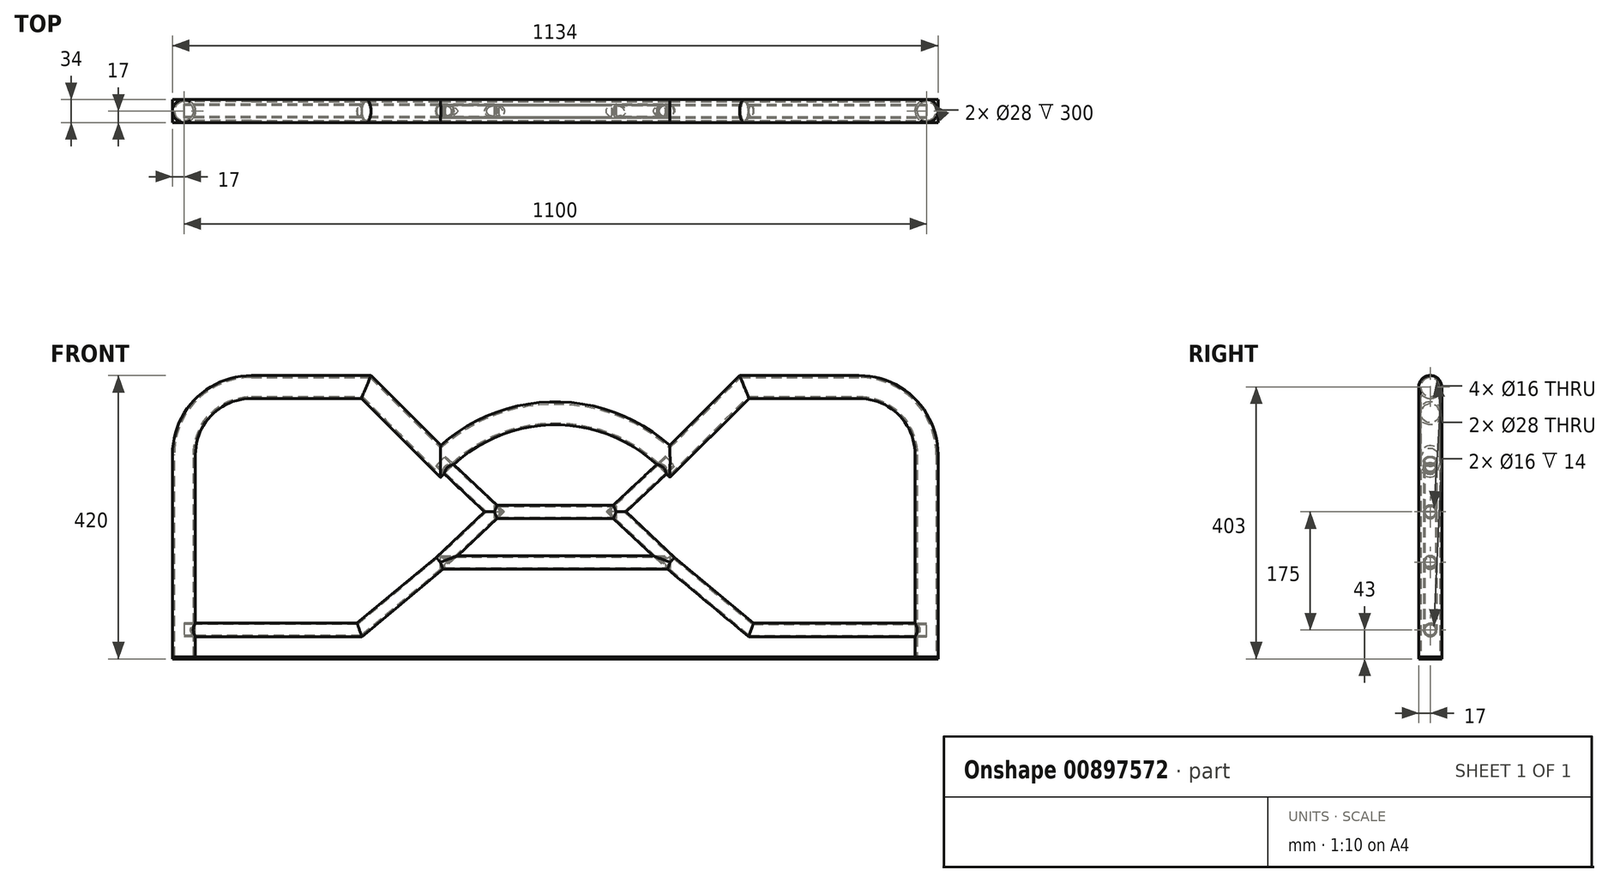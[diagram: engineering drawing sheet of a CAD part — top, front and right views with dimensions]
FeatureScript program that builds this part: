
annotation { "Feature Type Name" : "Feature", "Feature Type Description" : "" }
export const myFeature = defineFeature(function(context is Context, id is Id, definition is map)
    precondition{}
    {
        {
            var Q0;
            Q0=qCreatedBy(makeId("Front.planeOp"),FACE);
            var sketch = newSketch(context, id + "F0", { "sketchPlane" : qUnion([Q0])});
            skLineSegment(sketch, "E0", {"start": v(0, 0) * mm, "end": v(1100, 0) * mm, "construction": true});
            skLineSegment(sketch, "E1", {"start": v(0, 0) * mm, "end": v(0, 300) * mm});
            skLineSegment(sketch, "E2", {"start": v(1100, 0) * mm, "end": v(1100, 300) * mm});
            skLineSegment(sketch, "E3", {"start": v(550, 400) * mm, "end": v(550, 0) * mm, "construction": true});
            skLineSegment(sketch, "E4", {"start": v(550, 290) * mm, "end": v(380, 290) * mm, "construction": true});
            skLineSegment(sketch, "E5", {"start": v(550, 290) * mm, "end": v(720, 290) * mm, "construction": true});
            skLineSegment(sketch, "E6", {"start": v(380, 290) * mm, "end": v(270, 400) * mm});
            skArc(sketch, "E7", {"start": v(720, 290) * mm, "mid": v(550, 361) * mm, "end": v(380, 290) * mm});
            skLineSegment(sketch, "E8.MirrorCS", {"start": v(720, 290) * mm, "end": v(830, 400) * mm});
            skLineSegment(sketch, "E9", {"start": v(550, 140) * mm, "end": v(380, 140) * mm});
            skLineSegment(sketch, "E10", {"start": v(550, 140) * mm, "end": v(720, 140) * mm});
            skLineSegment(sketch, "E11", {"start": v(380, 140) * mm, "end": v(260, 40) * mm});
            skLineSegment(sketch, "E12", {"start": v(720, 140) * mm, "end": v(840, 40) * mm});
            skLineSegment(sketch, "E13", {"start": v(260, 40) * mm, "end": v(0, 40) * mm});
            skLineSegment(sketch, "E14", {"start": v(840, 40) * mm, "end": v(1100, 40) * mm});
            skLineSegment(sketch, "E15", {"start": v(100, 400) * mm, "end": v(270, 400) * mm});
            skLineSegment(sketch, "E16", {"start": v(1000, 400) * mm, "end": v(830, 400) * mm});
            skLineSegment(sketch, "E17", {"start": v(270, 400) * mm, "end": v(830, 400) * mm, "construction": true});
            skPoint(sketch, "E18.visualSharp", {"position": v(0, 400) * mm});
            skArc(sketch, "E18.filletArc", {"start": v(100, 400) * mm, "mid": v(29.29, 370.71) * mm, "end": v(0, 300) * mm});
            skPoint(sketch, "E19.visualSharp", {"position": v(1100, 400) * mm});
            skArc(sketch, "E19.filletArc", {"start": v(1100, 300) * mm, "mid": v(1070.71, 370.71) * mm, "end": v(1000, 400) * mm});
            skLineSegment(sketch, "E20", {"start": v(550, 215) * mm, "end": v(640, 215) * mm});
            skLineSegment(sketch, "E21", {"start": v(550, 215) * mm, "end": v(460, 215) * mm});
            skLineSegment(sketch, "E22", {"start": v(380, 290) * mm, "end": v(460, 215) * mm});
            skLineSegment(sketch, "E23", {"start": v(380, 140) * mm, "end": v(460, 215) * mm});
            skLineSegment(sketch, "E24", {"start": v(720, 290) * mm, "end": v(640, 215) * mm});
            skLineSegment(sketch, "E25", {"start": v(720, 140) * mm, "end": v(640, 215) * mm});
            skSolve(sketch);
        }
        {
            var Q0;
            Q0=sQuery(id+"F0.wireOp",EDGE,"E1");
            cPlane(context, id + "F1", {"entities" : qUnion([Q0]), "cplaneType" : CPlaneType.MID_PLANE, "offset" : 25 * mm, "width" : 150 * mm, "height" : 150 * mm});
        }
        {
            var Q0;
            Q0=qCreatedBy(id+"F1.planeOp",FACE);
            var sketch = newSketch(context, id + "F2", { "sketchPlane" : qUnion([Q0])});
            skCircle(sketch, "E26", {"center": v(0, 0) * mm, "radius": 17 * mm});
            skCircle(sketch, "E27", {"center": v(0, 0) * mm, "radius": 14 * mm});
            skSolve(sketch);
        }
        {
            var Q0;
            Q0=makeQuery(id+"F2.imprint","IMPRINT",FACE,{"disambiguationData":[TD([[makeQuery(id+"F2.imprint","IMPRINT",EDGE,{"derivedFrom":sQuery(id+"F2.wireOp",EDGE,"E26")}),1.0]])]});
            var Q1;
            Q1=sQuery(id+"F0.wireOp",EDGE,"E1");
            var Q2;
            Q2=sQuery(id+"F0.wireOp",EDGE,"E18.filletArc");
            var Q3;
            Q3=sQuery(id+"F0.wireOp",EDGE,"E15");
            var Q4;
            Q4=sQuery(id+"F0.wireOp",EDGE,"E6");
            var Q5;
            Q5=sQuery(id+"F0.wireOp",EDGE,"E7");
            var Q6;
            Q6=sQuery(id+"F0.wireOp",EDGE,"E8.MirrorCS");
            var Q7;
            Q7=sQuery(id+"F0.wireOp",EDGE,"E16");
            var Q8;
            Q8=sQuery(id+"F0.wireOp",EDGE,"E19.filletArc");
            var Q9;
            Q9=sQuery(id+"F0.wireOp",EDGE,"E2");
            sweep(context, id + "F3", {"profiles" : qUnion([Q0]), "path" : qUnion([Q1, Q2, Q3, Q4, Q5, Q6, Q7, Q8, Q9])});
        }
        {
            var Q0;
            Q0=sQuery(id+"F0.wireOp",EDGE,"E13");
            cPlane(context, id + "F4", {"entities" : qUnion([Q0]), "cplaneType" : CPlaneType.MID_PLANE, "offset" : 25 * mm, "width" : 150 * mm, "height" : 150 * mm});
        }
        {
            var Q0;
            Q0=qCreatedBy(id+"F4.planeOp",FACE);
            var sketch = newSketch(context, id + "F5", { "sketchPlane" : qUnion([Q0])});
            skCircle(sketch, "E28", {"center": v(0, 40) * mm, "radius": 10 * mm});
            skCircle(sketch, "E29", {"center": v(0, 40) * mm, "radius": 8 * mm});
            skSolve(sketch);
        }
        {
            var Q0;
            Q0=makeQuery(id+"F5.imprint","IMPRINT",FACE,{"disambiguationData":[TD([[makeQuery(id+"F5.imprint","IMPRINT",EDGE,{"derivedFrom":sQuery(id+"F5.wireOp",EDGE,"E28")}),1.0]])]});
            var Q1;
            Q1=sQuery(id+"F0.wireOp",EDGE,"E13");
            var Q2;
            Q2=sQuery(id+"F0.wireOp",EDGE,"E11");
            var Q3;
            Q3=sQuery(id+"F0.wireOp",EDGE,"E23");
            var Q4;
            Q4=sQuery(id+"F0.wireOp",EDGE,"E22");
            sweep(context, id + "F6", {"profiles" : qUnion([Q0]), "path" : qUnion([Q1, Q2, Q3, Q4])});
        }
        {
            var Q0;
            Q0=sQuery(id+"F0.wireOp",EDGE,"E14");
            cPlane(context, id + "F7", {"entities" : qUnion([Q0]), "cplaneType" : CPlaneType.MID_PLANE, "offset" : 25 * mm, "width" : 150 * mm, "height" : 150 * mm});
        }
        {
            var Q0;
            Q0=sQuery(id+"F0.wireOp",VERTEX,"E9.start");
            var Q1;
            Q1=sQuery(id+"F0.wireOp",EDGE,"E10");
            cPlane(context, id + "F8", {"entities" : qUnion([Q0, Q1]), "cplaneType" : CPlaneType.LINE_POINT, "offset" : 25 * mm, "width" : 150 * mm, "height" : 150 * mm});
        }
        {
            var Q0;
            Q0=qCreatedBy(id+"F8.planeOp",FACE);
            var sketch = newSketch(context, id + "F9", { "sketchPlane" : qUnion([Q0])});
            skCircle(sketch, "E30", {"center": v(0, 140) * mm, "radius": 10 * mm});
            skCircle(sketch, "E31", {"center": v(0, 140) * mm, "radius": 8 * mm});
            skSolve(sketch);
        }
        {
            var Q0;
            Q0=makeQuery(id+"F9.imprint","IMPRINT",FACE,{"disambiguationData":[TD([[makeQuery(id+"F9.imprint","IMPRINT",EDGE,{"derivedFrom":sQuery(id+"F9.wireOp",EDGE,"E30")}),1.0]])]});
            var Q1;
            Q1=sQuery(id+"F0.wireOp",EDGE,"E9");
            var Q2;
            Q2=sQuery(id+"F0.wireOp",EDGE,"E10");
            sweep(context, id + "F10", {"operationType" : NewBodyOperationType.ADD, "profiles" : qUnion([Q0]), "path" : qUnion([Q1, Q2])});
        }
        {
            var Q0;
            Q0=qCreatedBy(id+"F8.planeOp",FACE);
            var sketch = newSketch(context, id + "F11", { "sketchPlane" : qUnion([Q0])});
            skCircle(sketch, "E32", {"center": v(0, 215) * mm, "radius": 10 * mm});
            skCircle(sketch, "E33", {"center": v(0, 215) * mm, "radius": 8 * mm});
            skSolve(sketch);
        }
        {
            var Q0;
            Q0=makeQuery(id+"F11.imprint","IMPRINT",FACE,{"disambiguationData":[TD([[makeQuery(id+"F11.imprint","IMPRINT",EDGE,{"derivedFrom":sQuery(id+"F11.wireOp",EDGE,"E32")}),1.0]])]});
            var Q1;
            Q1=sQuery(id+"F0.wireOp",EDGE,"E21");
            var Q2;
            Q2=sQuery(id+"F0.wireOp",EDGE,"E20");
            sweep(context, id + "F12", {"operationType" : NewBodyOperationType.ADD, "profiles" : qUnion([Q0]), "path" : qUnion([Q1, Q2])});
        }
        {
            var Q0;
            Q0=qCreatedBy(id+"F7.planeOp",FACE);
            var sketch = newSketch(context, id + "F13", { "sketchPlane" : qUnion([Q0])});
            skCircle(sketch, "E34", {"center": v(0, 40) * mm, "radius": 10 * mm});
            skCircle(sketch, "E35", {"center": v(0, 40) * mm, "radius": 8 * mm});
            skSolve(sketch);
        }
        {
            var Q0;
            Q0=makeQuery(id+"F13.imprint","IMPRINT",FACE,{"disambiguationData":[TD([[makeQuery(id+"F13.imprint","IMPRINT",EDGE,{"derivedFrom":sQuery(id+"F13.wireOp",EDGE,"E34")}),1.0]])]});
            var Q1;
            Q1=sQuery(id+"F0.wireOp",EDGE,"E14");
            var Q2;
            Q2=sQuery(id+"F0.wireOp",EDGE,"E12");
            var Q3;
            Q3=sQuery(id+"F0.wireOp",EDGE,"E25");
            var Q4;
            Q4=sQuery(id+"F0.wireOp",EDGE,"E24");
            sweep(context, id + "F14", {"operationType" : NewBodyOperationType.ADD, "profiles" : qUnion([Q0]), "path" : qUnion([Q1, Q2, Q3, Q4])});
        }
        {
            var Q0;
            Q0=sQuery(id+"F0.wireOp",EDGE,"E0");
            cPlane(context, id + "F15", {"entities" : qUnion([Q0]), "cplaneType" : CPlaneType.LINE_ANGLE, "offset" : 25 * mm, "angle" : 90 * degree, "width" : 150 * mm, "height" : 150 * mm});
        }
        {
            var Q0;
            Q0=qCreatedBy(id+"F15.planeOp",FACE);
            var sketch = newSketch(context, id + "F16", { "sketchPlane" : qUnion([Q0])});
            skLineSegment(sketch, "E36.bottom", {"start": v(1117, 17) * mm, "end": v(-17, 17) * mm});
            skLineSegment(sketch, "E36.top", {"start": v(1117, -17) * mm, "end": v(-17, -17) * mm});
            skLineSegment(sketch, "E36.left", {"start": v(1117, 17) * mm, "end": v(1117, -17) * mm});
            skLineSegment(sketch, "E36.right", {"start": v(-17, 17) * mm, "end": v(-17, -17) * mm});
            skPoint(sketch, "E36.middle", {"position": v(550, 0) * mm});
            skLineSegment(sketch, "E37", {"start": v(0, -17) * mm, "end": v(0, 17) * mm, "construction": true});
            skSolve(sketch);
        }
        {
            var Q0;
            Q0 = qSketchRegion(id + "F16", true);
            extrude(context, id + "F17", {"entities" : qUnion([Q0]), "operationType" : NewBodyOperationType.ADD, "oppositeDirection" : true, "depth" : 3 * mm, "offsetDistance" : 25 * mm});
        }
    });
